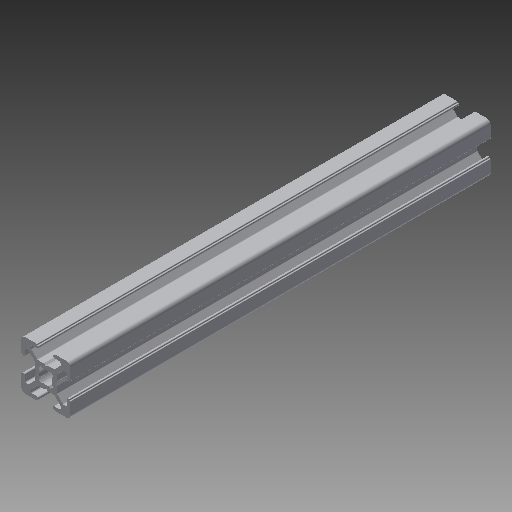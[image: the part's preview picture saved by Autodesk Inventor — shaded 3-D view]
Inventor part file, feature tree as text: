
AUTODESK INVENTOR PART (.ipt)
format: ipt  version: 2019 (Build 230136000, 136)  size: 315,904 bytes
history: native  units: in
note: dims shown in document units (in); Inventor stores cm internally (conversion verified against a paired STEP export)
features: other x3, extrude x1, sketch x1
ambient origin geometry x8: Origin, YZ Plane, XZ Plane, XY Plane, X Axis, Y Axis, Z Axis, Center Point
bodies: Solid1 (feature_tree)
feature tree (5):
  other  "Blocks"
  extrude  "Extrusion1"  Depth=1.0in
  sketch  "Sketch1"  dims[d1=0.0in d13=1.0in d14=1.0in]
  other  "20x20"
  other  "20x20:1"
